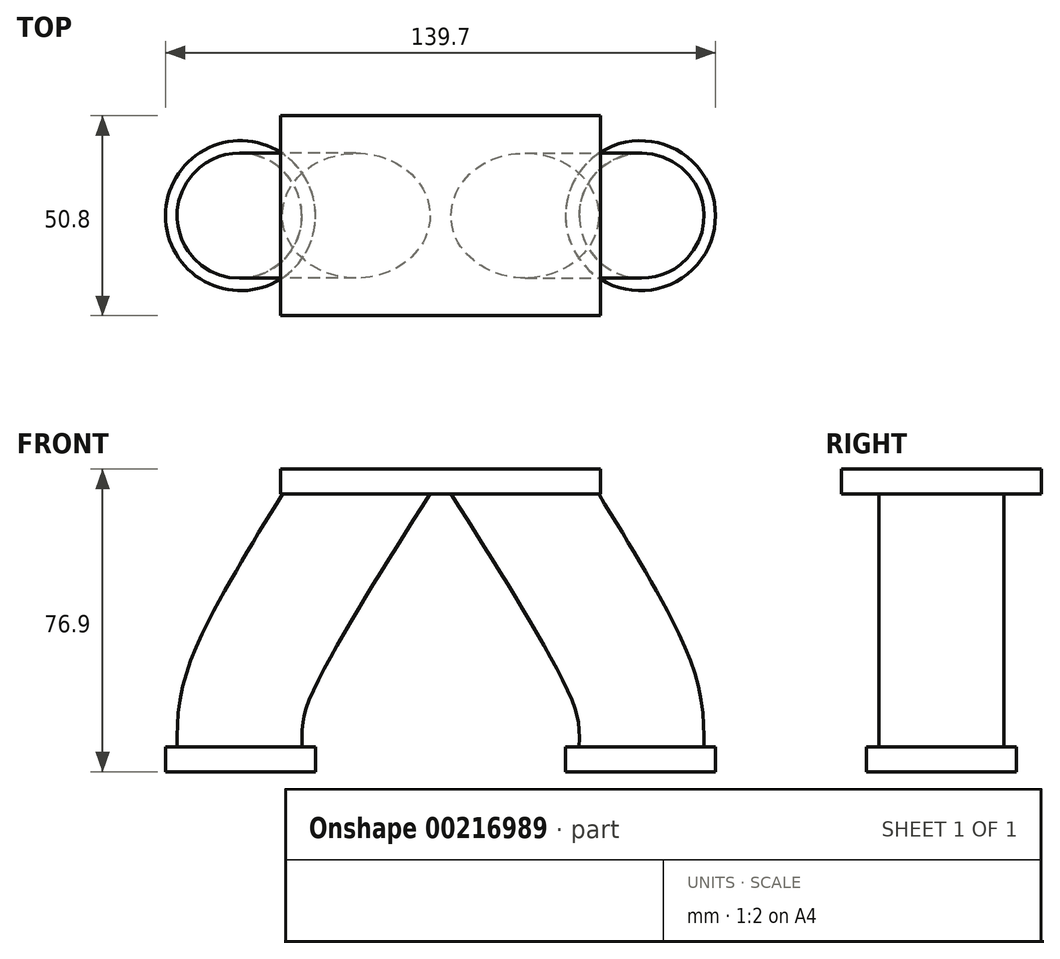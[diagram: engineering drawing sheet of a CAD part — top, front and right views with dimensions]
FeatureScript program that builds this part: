
annotation { "Feature Type Name" : "Feature", "Feature Type Description" : "" }
export const myFeature = defineFeature(function(context is Context, id is Id, definition is map)
    precondition{}
    {
        {
            var Q0;
            Q0=qCreatedBy(makeId("Top.planeOp"),FACE);
            var sketch = newSketch(context, id + "F0", { "sketchPlane" : qUnion([Q0])});
            skLineSegment(sketch, "E0", {"start": v(0, 0) * mm, "end": v(-50.8, 0) * mm});
            skLineSegment(sketch, "E1", {"start": v(0, 0) * mm, "end": v(50.8, 0) * mm});
            skCircle(sketch, "E2", {"center": v(-50.8, 0) * mm, "radius": 19.05 * mm});
            skCircle(sketch, "E3", {"center": v(50.8, 0) * mm, "radius": 19.05 * mm});
            skCircle(sketch, "E4", {"center": v(-50.8, 0) * mm, "radius": 15.88 * mm});
            skCircle(sketch, "E5", {"center": v(50.8, 0) * mm, "radius": 15.88 * mm});
            skSolve(sketch);
        }
        {
            var Q0;
            Q0=qCreatedBy(makeId("Front.planeOp"),FACE);
            var sketch = newSketch(context, id + "F1", { "sketchPlane" : qUnion([Q0])});
            skFitSpline(sketch, "E6", {"points": [v(-51.23, 0) * mm, v(-50.59, 17.6) * mm, v(-42.26, 36.82) * mm, v(-29.46, 58.6) * mm, v(-14.09, 82.92) * mm], "startDerivative": vector(-4.45, 80.48) * mm, "endDerivative": vector(56.14, 87.8) * mm});
            skFitSpline(sketch, "E7.MirrorCS", {"points": [v(51.23, 0) * mm, v(50.59, 17.6) * mm, v(42.26, 36.82) * mm, v(29.46, 58.6) * mm, v(14.09, 82.92) * mm], "startDerivative": vector(4.45, 80.48) * mm, "endDerivative": vector(-56.14, 87.8) * mm});
            skSolve(sketch);
        }
        {
            var Q0;
            Q0=makeQuery(id+"F0.imprint","IMPRINT",FACE,{"disambiguationData":[TD([[makeQuery(id+"F0.imprint","IMPRINT",EDGE,{"derivedFrom":sQuery(id+"F0.wireOp",EDGE,"E4")}),1.0]])]});
            var Q1;
            Q1=sQuery(id+"F1.wireOp",EDGE,"E6");
            sweep(context, id + "F2", {"profiles" : qUnion([Q0]), "path" : qUnion([Q1])});
        }
        {
            var Q0;
            Q0=makeQuery(id+"F2.opSweep","SWEPT_BODY",BODY,{"disambiguationData":[OSD([sQuery(id+"F0.wireOp",EDGE,"E4"),sQuery(id+"F1.wireOp",EDGE,"E6")])]});
            var Q1;
            Q1=qCreatedBy(makeId("Right.planeOp"),FACE);
            mirror(context, id + "F3", {"entities" : qUnion([Q0]), "mirrorPlane" : qUnion([Q1])});
        }
        {
            var Q0;
            Q0=qCreatedBy(makeId("Front.planeOp"),FACE);
            var sketch = newSketch(context, id + "F4", { "sketchPlane" : qUnion([Q0])});
            skLineSegment(sketch, "E8.bottom", {"start": v(40.64, 76.9) * mm, "end": v(-40.64, 76.9) * mm});
            skLineSegment(sketch, "E8.top", {"start": v(40.64, 70.55) * mm, "end": v(-40.64, 70.55) * mm});
            skLineSegment(sketch, "E8.left", {"start": v(40.64, 76.9) * mm, "end": v(40.64, 70.55) * mm});
            skLineSegment(sketch, "E8.right", {"start": v(-40.64, 76.9) * mm, "end": v(-40.64, 70.55) * mm});
            skPoint(sketch, "E8.middle", {"position": v(0, 73.72) * mm});
            skLineSegment(sketch, "E9", {"start": v(-40.64, 76.9) * mm, "end": v(-25.13, 101.08) * mm});
            skLineSegment(sketch, "E10", {"start": v(-25.13, 101.08) * mm, "end": v(31.68, 98.38) * mm});
            skLineSegment(sketch, "E11", {"start": v(31.68, 98.38) * mm, "end": v(40.64, 76.9) * mm});
            skSolve(sketch);
        }
        {
            var Q0;
            Q0 = qSketchRegion(id + "F4", true);
            extrude(context, id + "F5", {"entities" : qUnion([Q0]), "operationType" : NewBodyOperationType.ADD, "oppositeDirection" : true, "depth" : 50.8 * mm, "symmetric" : true});
        }
        {
            var Q0;
            Q0=makeQuery(id+"F4.imprint","IMPRINT",FACE,{"disambiguationData":[TD([[makeQuery(id+"F4.imprint","IMPRINT",EDGE,{"derivedFrom":sQuery(id+"F4.wireOp",EDGE,"E8.bottom")}),-1.0]])]});
            extrude(context, id + "F6", {"entities" : qUnion([Q0]), "operationType" : NewBodyOperationType.REMOVE, "oppositeDirection" : true, "depth" : 127 * mm, "symmetric" : true});
        }
        {
            var Q0;
            Q0=makeQuery(id+"F2.opSweep","CAP_FACE",FACE,{"disambiguationData":[OSD([sQuery(id+"F0.wireOp",EDGE,"E4"),sQuery(id+"F1.wireOp",VERTEX,"E6.start")])],"isStart":true});
            var sketch = newSketch(context, id + "F7", { "sketchPlane" : qUnion([Q0])});
            skCircle(sketch, "E12", {"center": v(-50.8, 0) * mm, "radius": 19.05 * mm});
            skSolve(sketch);
        }
        {
            var Q0;
            Q0 = qSketchRegion(id + "F7", true);
            extrude(context, id + "F8", {"entities" : qUnion([Q0]), "operationType" : NewBodyOperationType.ADD, "oppositeDirection" : true, "depth" : 6.35 * mm});
        }
        {
            var Q0;
            Q0=makeQuery(id+"F3.opPattern","COPY",FACE,{"derivedFrom":makeQuery(id+"F2.opSweep","CAP_FACE",FACE,{"disambiguationData":[OSD([sQuery(id+"F0.wireOp",EDGE,"E4"),sQuery(id+"F1.wireOp",VERTEX,"E6.start")])],"isStart":true}),"instanceName":"1"});
            var sketch = newSketch(context, id + "F9", { "sketchPlane" : qUnion([Q0])});
            skCircle(sketch, "E13", {"center": v(50.8, 0) * mm, "radius": 19.05 * mm});
            skSolve(sketch);
        }
        {
            var Q0;
            Q0 = qSketchRegion(id + "F9", true);
            extrude(context, id + "F10", {"entities" : qUnion([Q0]), "operationType" : NewBodyOperationType.ADD, "oppositeDirection" : true, "depth" : 6.35 * mm});
        }
    });
